FCSTD DOCUMENT  (FreeCAD 0.17R8039 (Git))
Label: cable_bushing_sketch
License: All rights reserved
LicenseURL: http://de.wikipedia.org/wiki/Alle_Rechte_vorbehalten
objects: Sketcher::SketchObject×1
note: 1 computed .brp shape members not serialized (recipe doc carries the construction recipe); baked Part::Feature solids carry a one-line shape summary decoded from their .brp

FEATURE [Sketcher::SketchObject] xsec_top
  sketch-geometry (3):
    g0: ArcOfCircle CenterX=-0.351322 CenterY=-0.109998 CenterZ=0 NormalX=0 NormalY=0 NormalZ=1 Radius=0.54 StartAngle=1.56835 EndAngle=2.93646
    g1: LineSegment StartX=-0.35 StartY=0.43 StartZ=0 EndX=-0.35 EndY=0 EndZ=0
    g2: LineSegment StartX=-0.35 StartY=0 StartZ=0 EndX=-0.88 EndY=0 EndZ=0
  constraints (10):
    c: PointOnObject(g0,g-1)
    c: PointOnObject(g1,g-1)
    c: Vertical(g1)
    c: Coincident(g1,g2)
    c: Coincident(g2,g0)
    c: Distance(g1) = 0.43  'D'
    c: Coincident(g0,g1)
    c: DistanceX(g0,g-1) = 0.35  'Bh'
    c: DistanceX(g0,g-1) = 0.88  'Ah'
    c: Radius(g0) = 0.54  'R'
